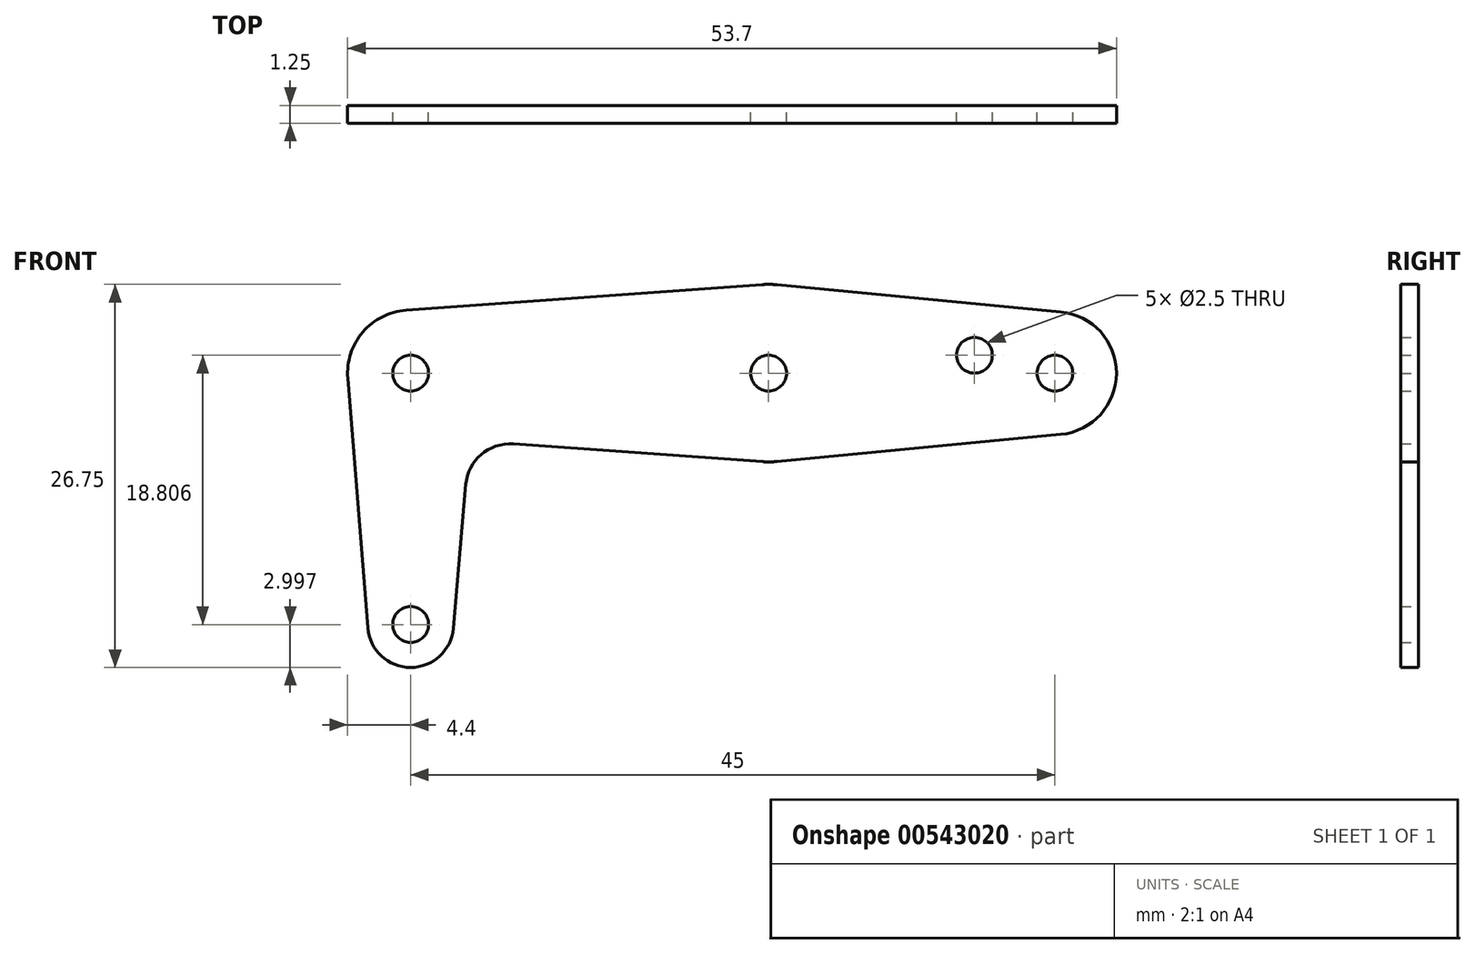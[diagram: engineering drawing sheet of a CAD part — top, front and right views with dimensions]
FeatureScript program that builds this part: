
annotation { "Feature Type Name" : "Feature", "Feature Type Description" : "" }
export const myFeature = defineFeature(function(context is Context, id is Id, definition is map)
    precondition{}
    {
        {
            var Q0;
            Q0=qCreatedBy(makeId("Front.planeOp"),FACE);
            var sketch = newSketch(context, id + "F0", { "sketchPlane" : qUnion([Q0])});
            skArc(sketch, "E0", {"start": v(-0.32, 14.88) * mm, "mid": v(-3.34, 13.36) * mm, "end": v(-4.39, 10.14) * mm});
            skArc(sketch, "E1", {"start": v(24.56, 4.3) * mm, "mid": v(25.08, 4.3) * mm, "end": v(25.59, 4.32) * mm});
            skArc(sketch, "E2", {"start": v(45.4, 6.21) * mm, "mid": v(49.3, 10.5) * mm, "end": v(45.4, 14.77) * mm});
            skArc(sketch, "E3", {"start": v(3.85, 2.72) * mm, "mid": v(4.93, 4.8) * mm, "end": v(7.16, 5.55) * mm});
            skLineSegment(sketch, "E4", {"start": v(-0.32, 14.88) * mm, "end": v(24.55, 16.68) * mm});
            skLineSegment(sketch, "E5", {"start": v(7.16, 5.55) * mm, "end": v(24.56, 4.3) * mm});
            skLineSegment(sketch, "E6", {"start": v(25.59, 4.32) * mm, "end": v(45.4, 6.21) * mm});
            skArc(sketch, "E7", {"start": v(-3, -7.3) * mm, "mid": v(0, -10.06) * mm, "end": v(2.99, -7.32) * mm});
            skLineSegment(sketch, "E8", {"start": v(-4.39, 10.14) * mm, "end": v(-3, -7.3) * mm});
            skLineSegment(sketch, "E9", {"start": v(3.85, 2.72) * mm, "end": v(2.99, -7.32) * mm});
            skCircle(sketch, "E10", {"center": v(39.38, 11.74) * mm, "radius": 1.25 * mm});
            skCircle(sketch, "E11", {"center": v(25, 10.5) * mm, "radius": 1.25 * mm});
            skCircle(sketch, "E12", {"center": v(0, 10.5) * mm, "radius": 1.25 * mm});
            skCircle(sketch, "E13", {"center": v(0, -7.06) * mm, "radius": 1.25 * mm});
            skCircle(sketch, "E14", {"center": v(45, 10.5) * mm, "radius": 1.25 * mm});
            skLineSegment(sketch, "E15", {"start": v(25.59, 16.66) * mm, "end": v(45.4, 14.77) * mm});
            skArc(sketch, "E16.trimOffspring", {"start": v(25.59, 16.66) * mm, "mid": v(25.07, 16.7) * mm, "end": v(24.55, 16.68) * mm});
            skSolve(sketch);
        }
        {
            var Q0;
            Q0 = qSketchRegion(id + "F0", true);
            extrude(context, id + "F1", {"entities" : qUnion([Q0]), "depth" : 1.25 * mm, "offsetDistance" : 25 * mm});
        }
    });
